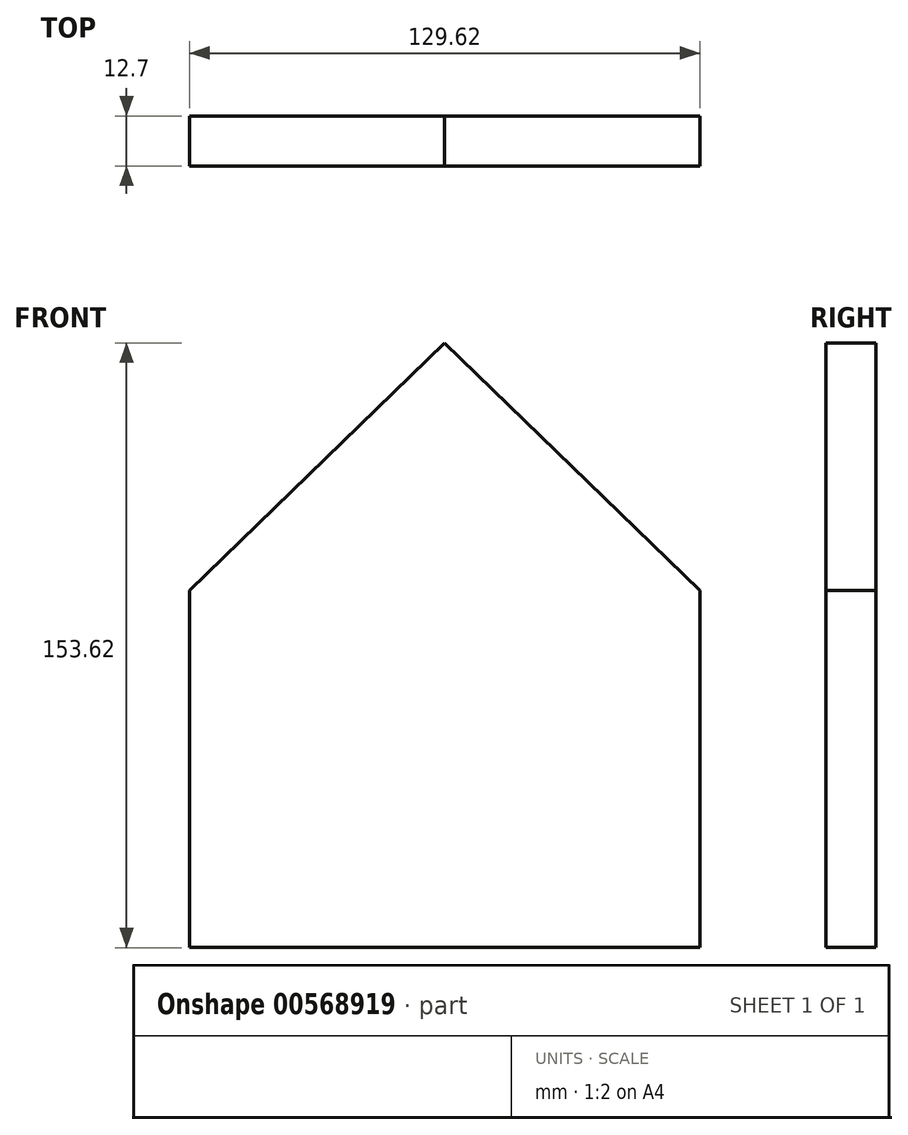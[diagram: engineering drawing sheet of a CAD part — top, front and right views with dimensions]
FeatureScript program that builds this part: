
annotation { "Feature Type Name" : "Feature", "Feature Type Description" : "" }
export const myFeature = defineFeature(function(context is Context, id is Id, definition is map)
    precondition{}
    {
        {
            var Q0;
            Q0=qCreatedBy(makeId("Front.planeOp"),FACE);
            var sketch = newSketch(context, id + "F0", { "sketchPlane" : qUnion([Q0])});
            skLineSegment(sketch, "E0", {"start": v(-64.81, -63.36) * mm, "end": v(-64.81, 27.44) * mm});
            skLineSegment(sketch, "E1", {"start": v(-64.81, -63.36) * mm, "end": v(64.81, -63.36) * mm});
            skLineSegment(sketch, "E2", {"start": v(64.81, -63.36) * mm, "end": v(64.81, 27.44) * mm});
            skLineSegment(sketch, "E3", {"start": v(-64.81, 27.44) * mm, "end": v(64.81, 27.44) * mm});
            skLineSegment(sketch, "E4", {"start": v(4.73, -63.36) * mm, "end": v(4.73, -12.56) * mm});
            skLineSegment(sketch, "E5", {"start": v(-39.9, -63.36) * mm, "end": v(-39.9, -12.56) * mm});
            skArc(sketch, "E6", {"start": v(-39.9, -12.56) * mm, "mid": v(-17.59, 9.75) * mm, "end": v(4.73, -12.56) * mm});
            skLineSegment(sketch, "E7", {"start": v(-64.81, 27.44) * mm, "end": v(0, 90.26) * mm});
            skLineSegment(sketch, "E8", {"start": v(64.81, 27.44) * mm, "end": v(0, 90.26) * mm});
            skSolve(sketch);
        }
        {
            var Q0;
            {var subQ0=sQuery(id+"F0.wireOp",EDGE,"E4");Q0=makeQuery(id+"F0.imprint","IMPRINT",FACE,{"disambiguationData":[TD([[makeQuery(id+"F0.imprint","IMPRINT",EDGE,{"derivedFrom":subQ0}),1.0]])]});}
            var Q1;
            Q1=makeQuery(id+"F0.imprint","IMPRINT",FACE,{"disambiguationData":[TD([[makeQuery(id+"F0.imprint","IMPRINT",EDGE,{"derivedFrom":sQuery(id+"F0.wireOp",EDGE,"E3")}),1.0]])]});
            var Q2;
            {var subQ3=sQuery(id+"F0.wireOp",EDGE,"E0");Q2=makeQuery(id+"F0.imprint","IMPRINT",FACE,{"disambiguationData":[TD([[makeQuery(id+"F0.imprint","IMPRINT",EDGE,{"derivedFrom":subQ3}),-1.0]])]});}
            extrude(context, id + "F1", {"entities" : qUnion([Q0, Q1, Q2]), "endBound" : BoundingType.SYMMETRIC, "depth" : 12.7 * mm, "offsetDistance" : 25.4 * mm});
        }
    });
